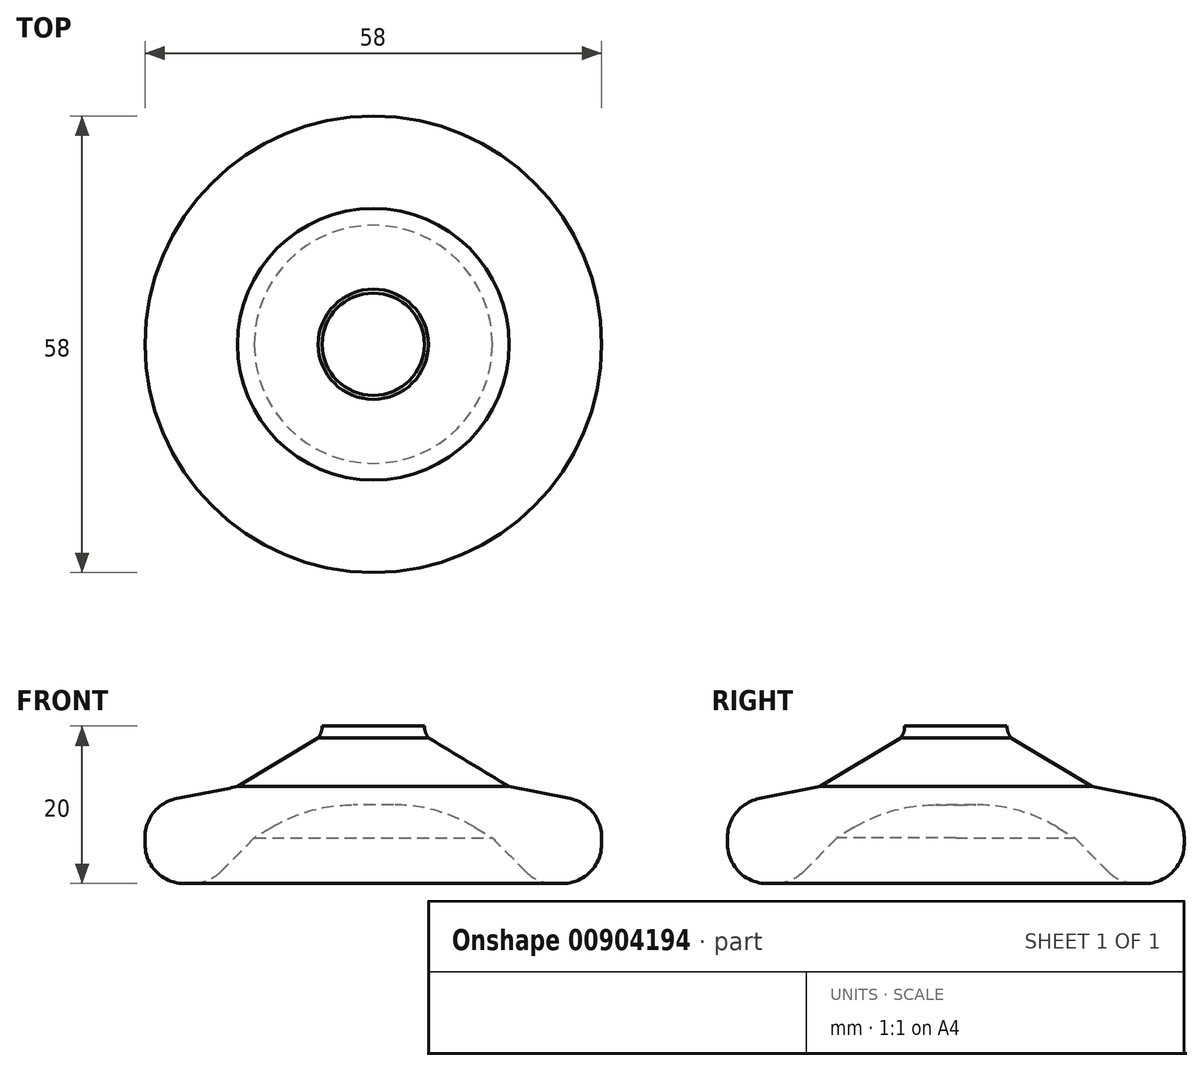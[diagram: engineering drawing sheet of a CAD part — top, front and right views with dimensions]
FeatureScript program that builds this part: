
annotation { "Feature Type Name" : "Feature", "Feature Type Description" : "" }
export const myFeature = defineFeature(function(context is Context, id is Id, definition is map)
    precondition{}
    {
        {
            var Q0;
            Q0=qCreatedBy(makeId("Front.planeOp"),FACE);
            var sketch = newSketch(context, id + "F0", { "sketchPlane" : qUnion([Q0])});
            skLineSegment(sketch, "E0", {"start": v(0, 0) * mm, "end": v(0, -10) * mm});
            skLineSegment(sketch, "E1", {"start": v(0, 0) * mm, "end": v(37.55, 0) * mm, "construction": true});
            skLineSegment(sketch, "E2", {"start": v(20.85, -20) * mm, "end": v(29, -20) * mm});
            skLineSegment(sketch, "E3", {"start": v(29, -20) * mm, "end": v(29, -10) * mm});
            skLineSegment(sketch, "E4", {"start": v(6.5, 0) * mm, "end": v(0, 0) * mm});
            skLineSegment(sketch, "E5", {"start": v(7, -1.5) * mm, "end": v(17.25, -7.69) * mm});
            skLineSegment(sketch, "E6", {"start": v(17.25, -7.69) * mm, "end": v(29, -10) * mm});
            skLineSegment(sketch, "E7", {"start": v(0, -10) * mm, "end": v(8.15, -10) * mm});
            skLineSegment(sketch, "E8", {"start": v(8.15, -10) * mm, "end": v(15.12, -14.21) * mm});
            skLineSegment(sketch, "E9", {"start": v(15.12, -14.21) * mm, "end": v(20.85, -20) * mm});
            skArc(sketch, "E10", {"start": v(6.5, 0) * mm, "mid": v(6.63, -0.8) * mm, "end": v(7, -1.5) * mm});
            skSolve(sketch);
        }
        {
            var Q0;
            Q0=makeQuery(id+"F0.imprint","IMPRINT",FACE,{"disambiguationData":[TD([[makeQuery(id+"F0.imprint","IMPRINT",EDGE,{"derivedFrom":sQuery(id+"F0.wireOp",EDGE,"E0")}),1.0]])]});
            var Q1;
            Q1=sQuery(id+"F0.wireOp",EDGE,"E0");
            revolve(context, id + "F1", {"surfaceOperationType" : NewSurfaceOperationType.NEW, "entities" : qUnion([Q0]), "axis" : qUnion([Q1]), "revolveType" : RevolveType.FULL});
        }
        {
            var Q0;
            Q0=makeQuery(id+"F1.opRevolve","SWEPT_EDGE",EDGE,{"disambiguationData":[OSD([sQuery(id+"F0.wireOp",EDGE,"E3"),sQuery(id+"F0.wireOp",EDGE,"E6")])]});
            var Q1;
            Q1=makeQuery(id+"F1.opRevolve","SWEPT_EDGE",EDGE,{"disambiguationData":[OSD([sQuery(id+"F0.wireOp",EDGE,"E2"),sQuery(id+"F0.wireOp",EDGE,"E3")])]});
            var Q2;
            Q2=makeQuery(id+"F1.opRevolve","SWEPT_EDGE",EDGE,{"disambiguationData":[OSD([sQuery(id+"F0.wireOp",EDGE,"E2"),sQuery(id+"F0.wireOp",EDGE,"E9")])]});
            fillet(context, id + "F2", {"entities" : qUnion([Q0, Q1, Q2]), "radius" : 5 * mm, "tangentPropagation" : true, "allowEdgeOverflow" : false});
        }
        {
            var Q0;
            Q0=makeQuery(id+"F1.opRevolve","SWEPT_EDGE",EDGE,{"disambiguationData":[OSD([sQuery(id+"F0.wireOp",EDGE,"E7"),sQuery(id+"F0.wireOp",EDGE,"E8")])]});
            fillet(context, id + "F3", {"entities" : qUnion([Q0]), "radius" : 20 * mm, "tangentPropagation" : true, "allowEdgeOverflow" : false});
        }
    });
